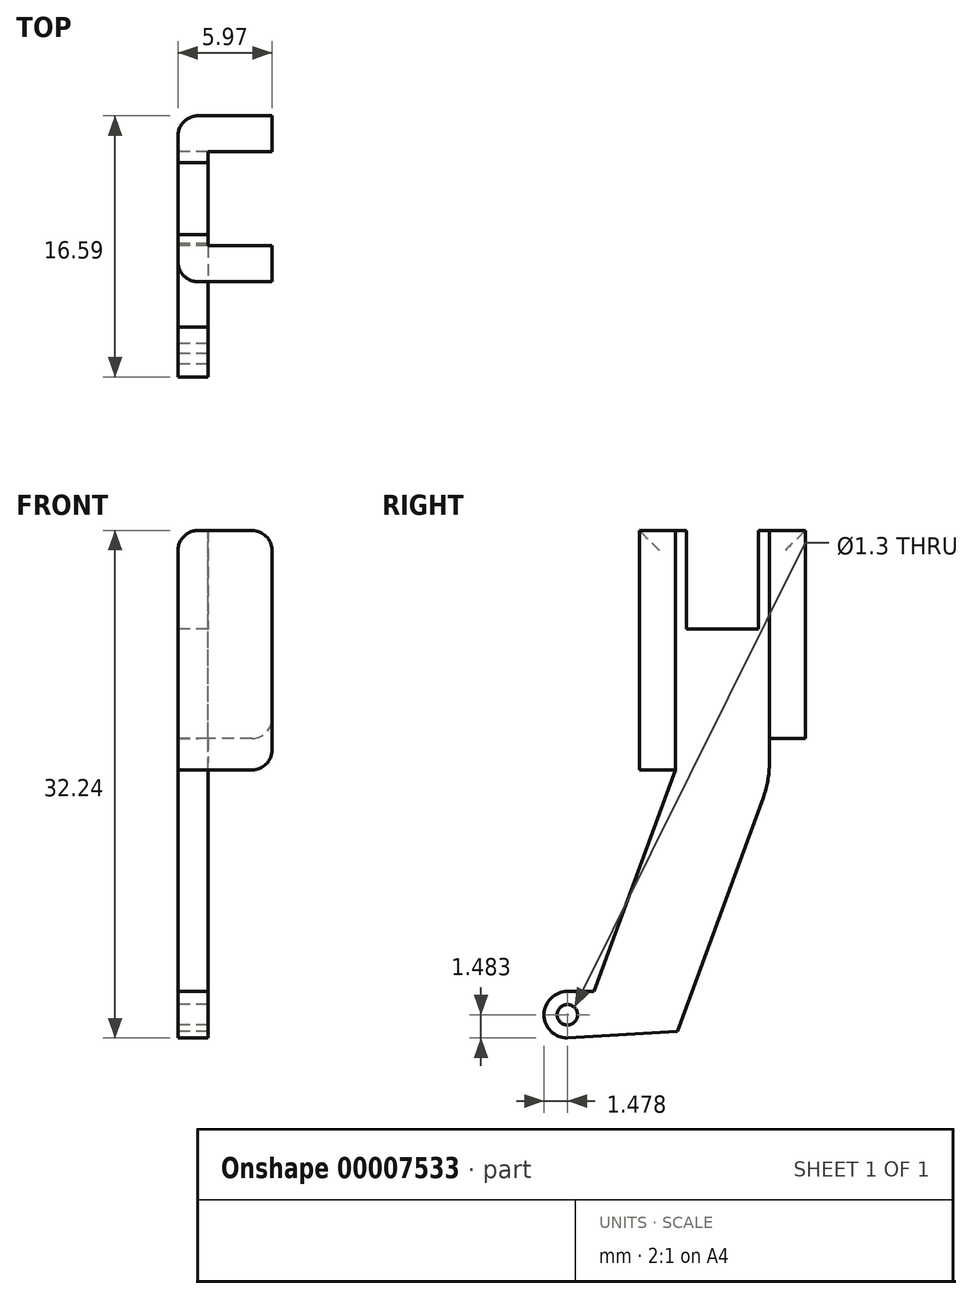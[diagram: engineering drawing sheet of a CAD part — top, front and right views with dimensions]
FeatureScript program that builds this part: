
annotation { "Feature Type Name" : "Feature", "Feature Type Description" : "" }
export const myFeature = defineFeature(function(context is Context, id is Id, definition is map)
    precondition{}
    {
        {
            var Q0;
            Q0=qCreatedBy(makeId("Right.planeOp"),FACE);
            var sketch = newSketch(context, id + "F0", { "sketchPlane" : qUnion([Q0])});
            skLineSegment(sketch, "E0", {"start": v(-2.29, 3.96) * mm, "end": v(-2.29, -2.29) * mm});
            skLineSegment(sketch, "E1", {"start": v(-2.29, -2.29) * mm, "end": v(2.29, -2.29) * mm});
            skLineSegment(sketch, "E2", {"start": v(-5.27, 3.96) * mm, "end": v(-2.29, 3.96) * mm});
            skLineSegment(sketch, "E3.0.MirrorCS", {"start": v(2.29, 3.96) * mm, "end": v(2.29, -2.29) * mm});
            skLineSegment(sketch, "E4.0.MirrorCS", {"start": v(5.27, 3.96) * mm, "end": v(5.27, -9.25) * mm});
            skLineSegment(sketch, "E5.trimOffspring", {"start": v(2.29, 3.96) * mm, "end": v(5.27, 3.96) * mm});
            skLineSegment(sketch, "E6", {"start": v(-5.27, 3.96) * mm, "end": v(-5.27, -11.25) * mm});
            skLineSegment(sketch, "E7", {"start": v(-2.98, 7.16) * mm, "end": v(-2.98, -13.67) * mm});
            skLineSegment(sketch, "E8.0.MirrorCS", {"start": v(2.98, 7.16) * mm, "end": v(2.98, -13.67) * mm});
            skLineSegment(sketch, "E9", {"start": v(-9.84, 6.23) * mm, "end": v(-9.84, -29.14) * mm, "construction": true});
            skLineSegment(sketch, "E10", {"start": v(-23.05, -26.8) * mm, "end": v(11.74, -26.8) * mm, "construction": true});
            skCircle(sketch, "E11", {"center": v(-9.84, -26.8) * mm, "radius": 0.65 * mm});
            skLineSegment(sketch, "E12", {"start": v(7.94, -11.25) * mm, "end": v(-7.63, -11.25) * mm, "construction": true});
            skLineSegment(sketch, "E13", {"start": v(-2.98, -11.25) * mm, "end": v(-8.14, -25.32) * mm});
            skArc(sketch, "E14", {"start": v(-9.84, -25.32) * mm, "mid": v(-11.32, -26.89) * mm, "end": v(-9.66, -28.27) * mm});
            skLineSegment(sketch, "E15.0", {"start": v(2.6, -13) * mm, "end": v(-2.85, -27.85) * mm});
            skLineSegment(sketch, "E16", {"start": v(5.27, -9.25) * mm, "end": v(2.98, -9.25) * mm});
            skLineSegment(sketch, "E17", {"start": v(2.98, -9.25) * mm, "end": v(2.98, -10.82) * mm});
            skPoint(sketch, "E18.visualSharp", {"position": v(2.98, -11.94) * mm});
            skArc(sketch, "E18.filletArc", {"start": v(2.6, -13) * mm, "mid": v(2.89, -11.93) * mm, "end": v(2.98, -10.82) * mm});
            skLineSegment(sketch, "E19", {"start": v(-9.84, -25.32) * mm, "end": v(-8.14, -25.32) * mm});
            skLineSegment(sketch, "E20", {"start": v(-9.84, -28.28) * mm, "end": v(-2.85, -27.85) * mm});
            skLineSegment(sketch, "E21", {"start": v(-2.98, -11.25) * mm, "end": v(-5.27, -11.25) * mm});
            skPoint(sketch, "E22.orphan", {"position": v(-8.2, -25.32) * mm});
            skPoint(sketch, "E23.orphan", {"position": v(-8.2, -25.48) * mm});
            skLineSegment(sketch, "E24", {"start": v(-2.98, 7.16) * mm, "end": v(2.98, 7.16) * mm});
            skLineSegment(sketch, "E25", {"start": v(-2.98, -13.67) * mm, "end": v(2.98, -13.67) * mm});
            skSolve(sketch);
        }
        {
            var Q0;
            {var subQ14=sQuery(id+"F0.wireOp",EDGE,"E0");Q0=makeQuery(id+"F0.imprint","IMPRINT",FACE,{"disambiguationData":[TD([[makeQuery(id+"F0.imprint","IMPRINT",EDGE,{"derivedFrom":subQ14}),-1.0]])]});}
            var Q1;
            Q1=makeQuery(id+"F0.imprint","IMPRINT",FACE,{"disambiguationData":[TD([[makeQuery(id+"F0.imprint","IMPRINT",EDGE,{"derivedFrom":sQuery(id+"F0.wireOp",EDGE,"E11")}),-1.0]])]});
            var Q2;
            {var subQ4=sQuery(id+"F0.wireOp",EDGE,"E4.0.MirrorCS");Q2=makeQuery(id+"F0.imprint","IMPRINT",FACE,{"disambiguationData":[TD([[makeQuery(id+"F0.imprint","IMPRINT",EDGE,{"derivedFrom":subQ4}),-1.0]])]});}
            var Q3;
            {var subQ4=sQuery(id+"F0.wireOp",EDGE,"E6");Q3=makeQuery(id+"F0.imprint","IMPRINT",FACE,{"disambiguationData":[TD([[makeQuery(id+"F0.imprint","IMPRINT",EDGE,{"derivedFrom":subQ4}),1.0]])]});}
            extrude(context, id + "F1", {"entities" : qUnion([Q0, Q1, Q2, Q3]), "depth" : 1.9 * mm});
        }
        {
            var Q0;
            {var subQ4=sQuery(id+"F0.wireOp",EDGE,"E4.0.MirrorCS");Q0=makeQuery(id+"F0.imprint","IMPRINT",FACE,{"disambiguationData":[TD([[makeQuery(id+"F0.imprint","IMPRINT",EDGE,{"derivedFrom":subQ4}),-1.0]])]});}
            var Q1;
            {var subQ4=sQuery(id+"F0.wireOp",EDGE,"E6");Q1=makeQuery(id+"F0.imprint","IMPRINT",FACE,{"disambiguationData":[TD([[makeQuery(id+"F0.imprint","IMPRINT",EDGE,{"derivedFrom":subQ4}),1.0]])]});}
            extrude(context, id + "F2", {"entities" : qUnion([Q0, Q1]), "operationType" : NewBodyOperationType.ADD, "depth" : 5.97 * mm});
        }
        {
            var Q0;
            Q0=makeQuery(id+"F2.opExtrude","CAP_EDGE",EDGE,{"disambiguationData":[OSD([sQuery(id+"F0.wireOp",EDGE,"E2")])],"isStart":false});
            var Q1;
            Q1=makeQuery(id+"F2.opExtrude","CAP_EDGE",EDGE,{"disambiguationData":[OSD([sQuery(id+"F0.wireOp",EDGE,"E5.trimOffspring")])],"isStart":false});
            var Q2;
            Q2=makeQuery(id+"F2.opExtrude","CAP_EDGE",EDGE,{"disambiguationData":[OSD([sQuery(id+"F0.wireOp",EDGE,"E21")])],"isStart":false});
            var Q3;
            Q3=makeQuery(id+"F2.opExtrude","CAP_EDGE",EDGE,{"disambiguationData":[OSD([sQuery(id+"F0.wireOp",EDGE,"E16")])],"isStart":false});
            var Q4;
            Q4=makeQuery(id+"F1.opExtrude","CAP_EDGE",EDGE,{"disambiguationData":[OSD([sQuery(id+"F0.wireOp",EDGE,"E2")])],"isStart":true});
            var Q5;
            Q5=makeQuery(id+"F1.opExtrude","CAP_EDGE",EDGE,{"disambiguationData":[OSD([sQuery(id+"F0.wireOp",EDGE,"E5.trimOffspring")])],"isStart":true});
            var Q6;
            Q6=makeQuery(id+"F1.opExtrude","CAP_EDGE",EDGE,{"disambiguationData":[OSD([sQuery(id+"F0.wireOp",EDGE,"E6")])],"isStart":true});
            var Q7;
            Q7=makeQuery(id+"F1.opExtrude","CAP_EDGE",EDGE,{"disambiguationData":[OSD([sQuery(id+"F0.wireOp",EDGE,"E4.0.MirrorCS")])],"isStart":true});
            fillet(context, id + "F3", {"entities" : qUnion([Q0, Q1, Q2, Q3, Q4, Q5, Q6, Q7]), "radius" : 1.27 * mm, "tangentPropagation" : true, "allowEdgeOverflow" : false});
        }
    });
